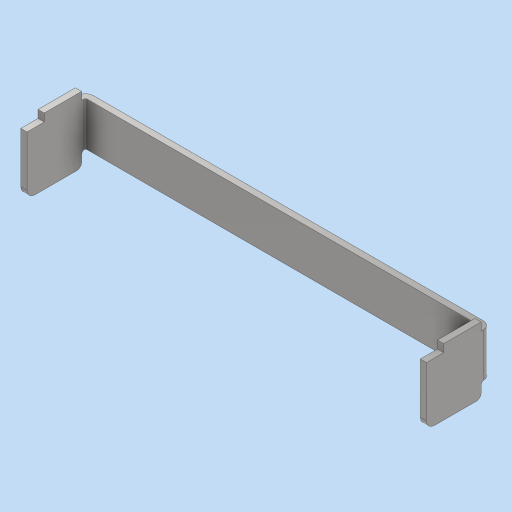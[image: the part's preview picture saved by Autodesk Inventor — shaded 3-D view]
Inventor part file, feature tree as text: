
AUTODESK INVENTOR PART (.ipt)
format: ipt  version: 2023 (Build 270158000, 158)  size: 293,888 bytes
history: native  units: mm
features: other x4, extrude x1
ambient origin geometry x8: Origin, YZ Plane, XZ Plane, XY Plane, X Axis, Y Axis, Z Axis, Center Point
bodies: Body1 (feature_tree)
feature tree (5):
  other  "實體1"
  extrude  "擠出1"  Depth=2.0mm TaperAngle=0.0deg
  other  "折彎零件1"
  other  "折彎零件2"
  other  "定義1"
